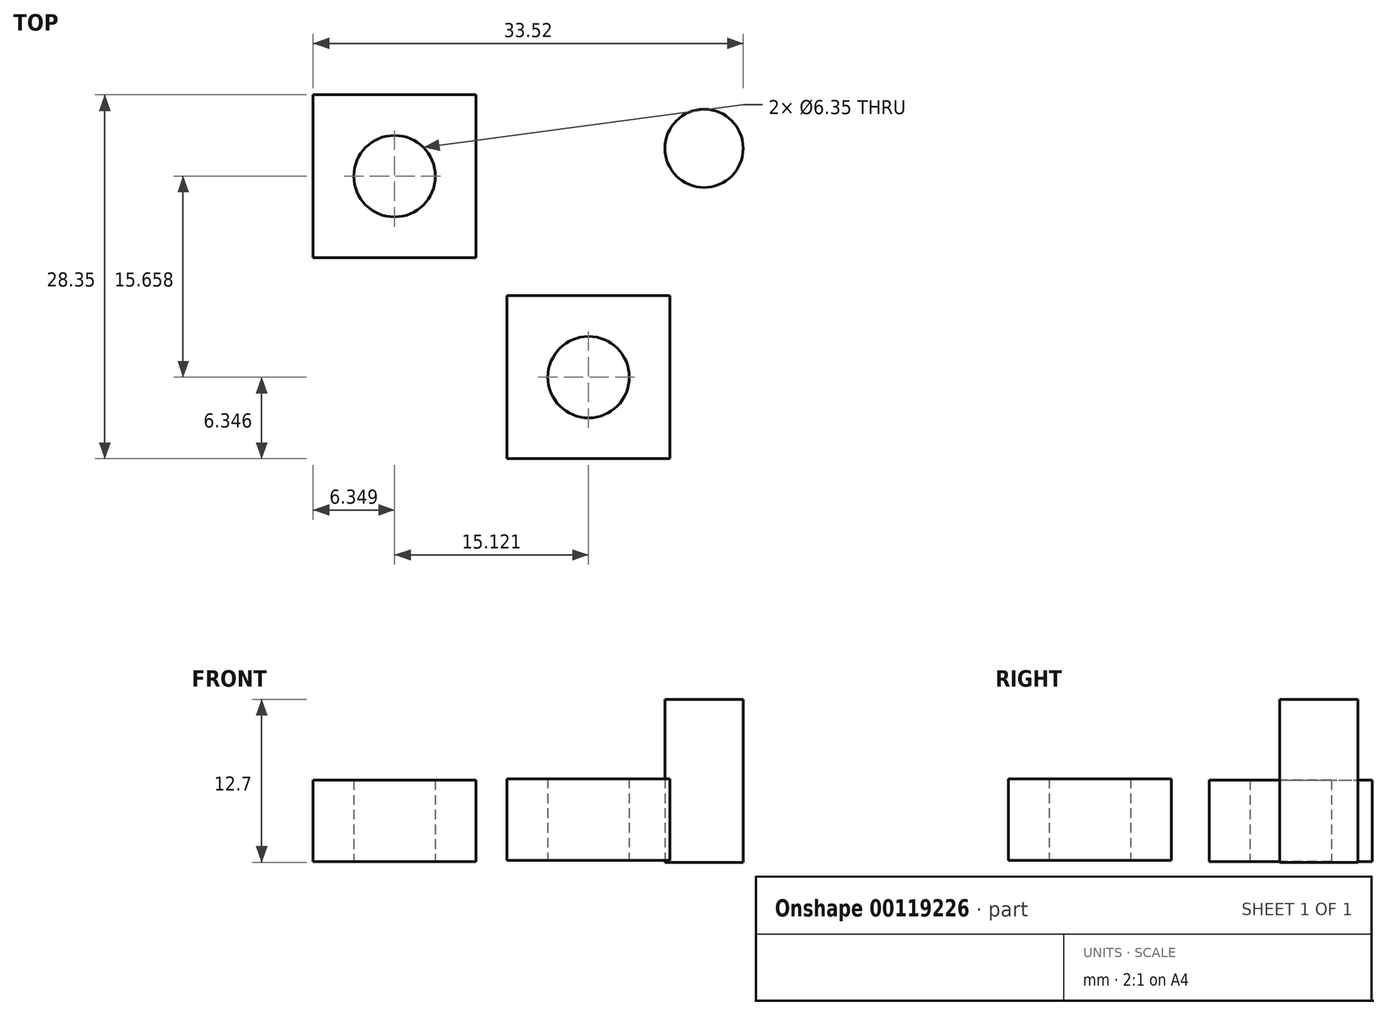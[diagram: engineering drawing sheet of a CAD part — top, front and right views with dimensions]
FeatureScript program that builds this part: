
annotation { "Feature Type Name" : "Feature", "Feature Type Description" : "" }
export const myFeature = defineFeature(function(context is Context, id is Id, definition is map)
    precondition{}
    {
        {
            var Q0;
            Q0=qCreatedBy(makeId("Top.planeOp"),FACE);
            var sketch = newSketch(context, id + "F0", { "sketchPlane" : qUnion([Q0])});
            skLineSegment(sketch, "E0.bottom", {"start": v(-50.3, 29) * mm, "end": v(-63, 29) * mm});
            skLineSegment(sketch, "E0.top", {"start": v(-50.3, 41.7) * mm, "end": v(-63, 41.7) * mm});
            skLineSegment(sketch, "E0.left", {"start": v(-50.3, 29) * mm, "end": v(-50.3, 41.7) * mm});
            skLineSegment(sketch, "E0.right", {"start": v(-63, 29) * mm, "end": v(-63, 41.7) * mm});
            skPoint(sketch, "E0.middle", {"position": v(-56.64, 35.35) * mm});
            skCircle(sketch, "E1", {"center": v(-56.64, 35.35) * mm, "radius": 3.17 * mm});
            skSolve(sketch);
        }
        {
            var Q0;
            Q0=makeQuery(id+"F0.imprint","IMPRINT",FACE,{"disambiguationData":[TD([[makeQuery(id+"F0.imprint","IMPRINT",EDGE,{"derivedFrom":sQuery(id+"F0.wireOp",EDGE,"E0.bottom")}),-1.0]])]});
            extrude(context, id + "F1", {"entities" : qUnion([Q0]), "endBound" : BoundingType.SYMMETRIC, "depth" : 6.35 * mm});
        }
        {
            var Q0;
            Q0=qCreatedBy(makeId("Top.planeOp"),FACE);
            var sketch = newSketch(context, id + "F2", { "sketchPlane" : qUnion([Q0])});
            skCircle(sketch, "E2", {"center": v(-32.52, 37.52) * mm, "radius": 3.05 * mm});
            skSolve(sketch);
        }
        {
            var Q0;
            Q0=makeQuery(id+"F2.imprint","IMPRINT",FACE,{"disambiguationData":[TD([[makeQuery(id+"F2.imprint","IMPRINT",EDGE,{"derivedFrom":sQuery(id+"F2.wireOp",EDGE,"E2")}),1.0]])]});
            extrude(context, id + "F3", {"entities" : qUnion([Q0]), "endBound" : BoundingType.SYMMETRIC, "depth" : 12.7 * mm});
        }
        {
            var Q0;
            Q0=qCreatedBy(makeId("Top.planeOp"),FACE);
            var sketch = newSketch(context, id + "F4", { "sketchPlane" : qUnion([Q0])});
            skLineSegment(sketch, "E3.bottom", {"start": v(-54.3, 13.35) * mm, "end": v(-67, 13.35) * mm});
            skLineSegment(sketch, "E3.top", {"start": v(-54.3, 26.05) * mm, "end": v(-67, 26.05) * mm});
            skLineSegment(sketch, "E3.left", {"start": v(-54.3, 13.35) * mm, "end": v(-54.3, 26.05) * mm});
            skLineSegment(sketch, "E3.right", {"start": v(-67, 13.35) * mm, "end": v(-67, 26.05) * mm});
            skPoint(sketch, "E3.middle", {"position": v(-60.64, 19.7) * mm});
            skCircle(sketch, "E4", {"center": v(-60.64, 19.7) * mm, "radius": 3.18 * mm});
            skSolve(sketch);
        }
        {
            var Q0;
            Q0=makeQuery(id+"F4.imprint","IMPRINT",FACE,{"disambiguationData":[TD([[makeQuery(id+"F4.imprint","IMPRINT",EDGE,{"derivedFrom":sQuery(id+"F4.wireOp",EDGE,"E3.bottom")}),-1.0]])]});
            extrude(context, id + "F5", {"entities" : qUnion([Q0]), "endBound" : BoundingType.SYMMETRIC, "depth" : 6.35 * mm});
        }
        {
            var Q0;
            Q0=makeQuery(id+"F5.opExtrude","SWEPT_BODY",BODY,{"disambiguationData":[OSD([sQuery(id+"F4.wireOp",EDGE,"E3.bottom"),sQuery(id+"F4.wireOp",EDGE,"E3.top"),sQuery(id+"F4.wireOp",EDGE,"E3.left"),sQuery(id+"F4.wireOp",EDGE,"E3.right"),sQuery(id+"F4.wireOp",EDGE,"E4")])]});
            var Q1;
            Q1=makeQuery(id+"F5.opExtrude","CAP_FACE",FACE,{"disambiguationData":[OSD([sQuery(id+"F4.wireOp",EDGE,"E3.bottom"),sQuery(id+"F4.wireOp",EDGE,"E3.top"),sQuery(id+"F4.wireOp",EDGE,"E3.left"),sQuery(id+"F4.wireOp",EDGE,"E3.right"),sQuery(id+"F4.wireOp",EDGE,"E4")])],"isStart":false});
            transform(context, id + "F6", {"entities" : qUnion([Q0]), "transformType" : TransformType.TRANSLATION_3D, "dx" : 19.12 * mm, "dy" : 0 * mm, "dz" : 3.2 * mm, "makeCopy" : false});
        }
        {
            var Q0;
            Q0=makeQuery(id+"F1.opExtrude","SWEPT_BODY",BODY,{"disambiguationData":[OSD([sQuery(id+"F0.wireOp",EDGE,"E0.bottom"),sQuery(id+"F0.wireOp",EDGE,"E0.top"),sQuery(id+"F0.wireOp",EDGE,"E0.left"),sQuery(id+"F0.wireOp",EDGE,"E0.right"),sQuery(id+"F0.wireOp",EDGE,"E1")])]});
            transform(context, id + "F7", {"entities" : qUnion([Q0]), "transformType" : TransformType.TRANSLATION_3D, "dx" : 0 * mm, "dy" : 0 * mm, "dz" : 3.08 * mm, "makeCopy" : false});
        }
        {
            var Q0;
            Q0=makeQuery(id+"F3.opExtrude","SWEPT_BODY",BODY,{"disambiguationData":[OSD([sQuery(id+"F2.wireOp",EDGE,"E2")])]});
            transform(context, id + "F8", {"entities" : qUnion([Q0]), "transformType" : TransformType.TRANSLATION_3D, "dx" : 0 * mm, "dy" : 0 * mm, "dz" : 6.22 * mm, "makeCopy" : false});
        }
    });
